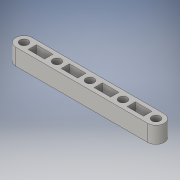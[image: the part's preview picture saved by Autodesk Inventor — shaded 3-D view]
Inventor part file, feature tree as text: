
AUTODESK INVENTOR PART (.ipt)
format: ipt  version: 2016 SP1 (Build 200210100, 210)  size: 157,184 bytes
history: native  units: in
note: dims shown in document units (in); Inventor stores cm internally (conversion verified against a paired STEP export)
features: extrude x3, sketch x3
ambient origin geometry x8: Origin, YZ Plane, XZ Plane, XY Plane, X Axis, Y Axis, Z Axis, Center Point
bodies: Solid1 (feature_tree)
feature tree (6):
  extrude  "Extrusion1"  Depth=0.25in
  extrude  "Extrusion2"  Depth=2.0in
  extrude  "Extrusion3"  Depth=0.5in
  sketch  "Sketch1"  dims[d2=4.0in d3=0.25in]
  sketch  "Sketch2"  dims[d4=0.25in d5=2.0in]
  sketch  "Sketch3"  dims[d6=0.0in d7=0.5in d8=4.0in d9=0.25in d10=0.5in d11=0.0in d12=0.25in d13=2.0in d14=0.0in d15=1.9685in d17=1.0in d18=0.3937in d20=1.0in d22=0.0in d23=0.0in d24=0.5in d25=0.25in d26=1.25in d27=0.125in d28=1.5748in d30=1.0in d31=0.3937in d33=1.0in d35=0.0in d36=0.0in]
